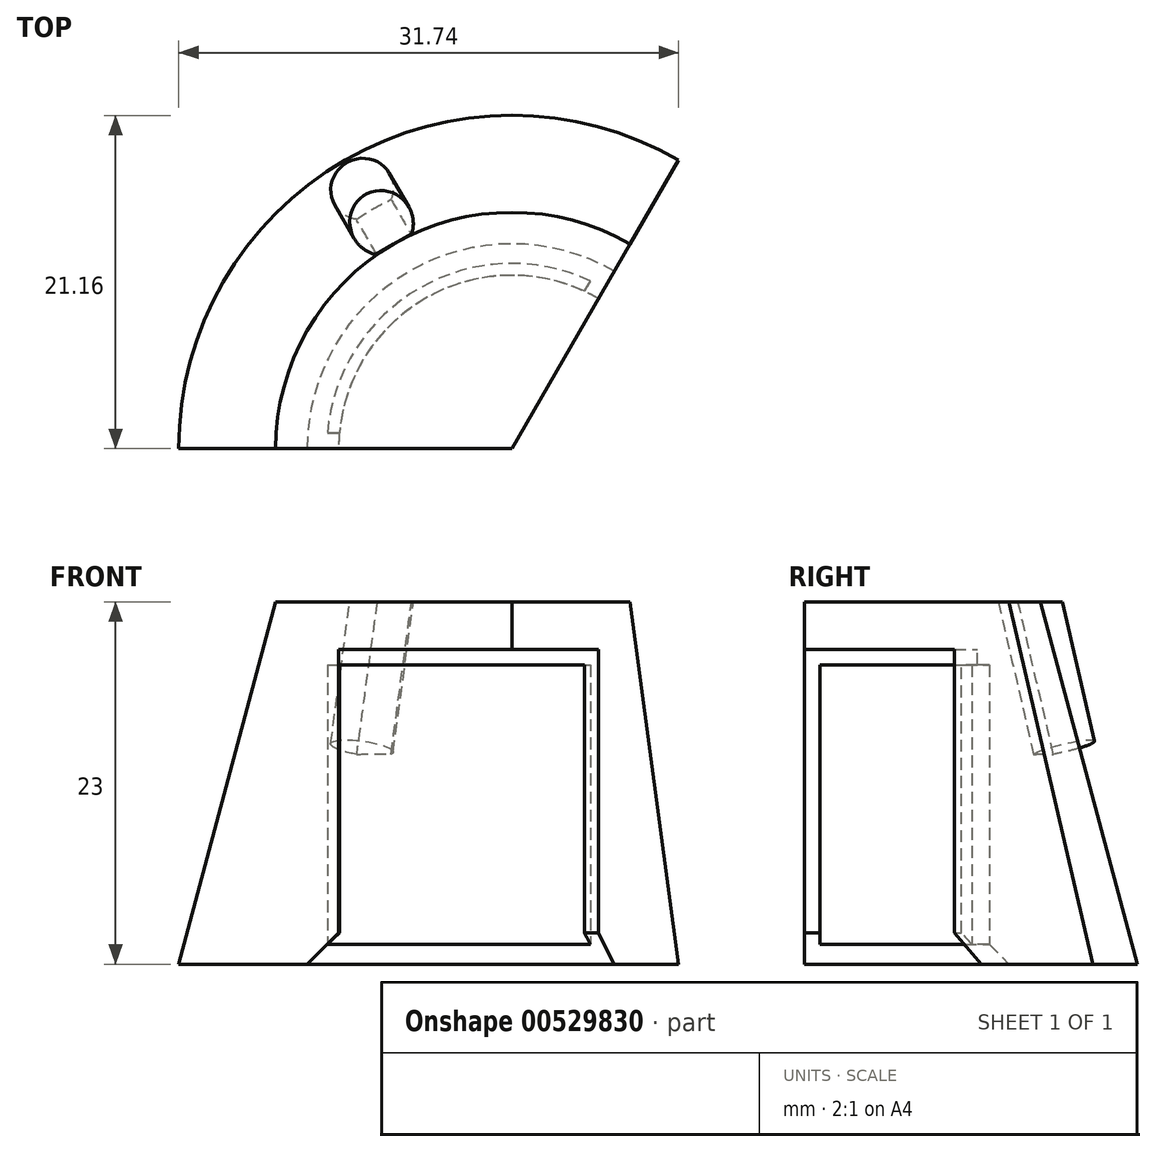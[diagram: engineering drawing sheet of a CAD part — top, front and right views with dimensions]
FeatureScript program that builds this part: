
annotation { "Feature Type Name" : "Feature", "Feature Type Description" : "" }
export const myFeature = defineFeature(function(context is Context, id is Id, definition is map)
    precondition{}
    {
        {
            var Q0;
            Q0=qCreatedBy(makeId("Front.planeOp"),FACE);
            var sketch = newSketch(context, id + "F0", { "sketchPlane" : qUnion([Q0])});
            skLineSegment(sketch, "E0", {"start": v(0, 0) * mm, "end": v(0, -3) * mm});
            skLineSegment(sketch, "E1", {"start": v(0, -3) * mm, "end": v(-11, -3) * mm});
            skLineSegment(sketch, "E2", {"start": v(-11, -3) * mm, "end": v(-11, -21) * mm});
            skLineSegment(sketch, "E3", {"start": v(0, 0) * mm, "end": v(-15, 0) * mm});
            skLineSegment(sketch, "E4", {"start": v(-13, -23) * mm, "end": v(-21.16, -23) * mm});
            skLineSegment(sketch, "E5", {"start": v(-15, 0) * mm, "end": v(-21.16, -23) * mm});
            skLineSegment(sketch, "E6", {"start": v(-11, -21) * mm, "end": v(-13, -23) * mm});
            skSolve(sketch);
        }
        {
            var Q0;
            Q0=makeQuery(id+"F0.imprint","IMPRINT",FACE,{"disambiguationData":[TD([[makeQuery(id+"F0.imprint","IMPRINT",EDGE,{"derivedFrom":sQuery(id+"F0.wireOp",EDGE,"E0")}),-1.0]])]});
            var Q1;
            Q1=sQuery(id+"F0.wireOp",EDGE,"E0");
            revolve(context, id + "F1", {"entities" : qUnion([Q0]), "axis" : qUnion([Q1]), "revolveType" : RevolveType.ONE_DIRECTION, "angle" : 120 * degree});
        }
        {
            var Q0;
            Q0=makeQuery(id+"F1.opRevolve","SWEPT_FACE",FACE,{"disambiguationData":[OSD([sQuery(id+"F0.wireOp",EDGE,"E3")])]});
            var sketch = newSketch(context, id + "F2", { "sketchPlane" : qUnion([Q0])});
            skLineSegment(sketch, "E7", {"start": v(-3.98, 15.02) * mm, "end": v(-11.37, 10.76) * mm, "construction": true});
            skLineSegment(sketch, "E8", {"start": v(-15, 0) * mm, "end": v(7.5, 13) * mm, "construction": true});
            skPoint(sketch, "E9", {"position": v(-7.5, 13) * mm});
            skSolve(sketch);
        }
        {
            var Q0;
            Q0=sQuery(id+"F2.wireOp",EDGE,"E7");
            var Q1;
            {var subQ0=sQuery(id+"F0.wireOp",EDGE,"E3");Q1=makeQuery(id+"F2.imprint","IMPRINT",FACE,{"disambiguationData":[TD([[makeQuery(id+"F2.imprint","IMPRINT",EDGE,{"derivedFrom":makeQuery(id+"F1.opRevolve","CAP_EDGE",EDGE,{"disambiguationData":[OSD([subQ0])],"isStart":true})}),-1.0]])]});}
            cPlane(context, id + "F3", {"entities" : qUnion([Q0, Q1]), "cplaneType" : CPlaneType.LINE_ANGLE, "offset" : 25 * mm, "angle" : 15 * degree, "oppositeDirection" : true, "width" : 150 * mm, "height" : 150 * mm});
        }
        {
            var Q0;
            Q0=qCreatedBy(id+"F3.planeOp",FACE);
            var sketch = newSketch(context, id + "F4", { "sketchPlane" : qUnion([Q0])});
            skPoint(sketch, "E10.0", {"position": v(-7.06, -12.65) * mm});
            skLineSegment(sketch, "E11", {"start": v(-7.06, -12.65) * mm, "end": v(-7.79, -13.96) * mm});
            skCircle(sketch, "E12", {"center": v(-7.79, -13.96) * mm, "radius": 2 * mm});
            skSolve(sketch);
        }
        {
            var Q0;
            Q0=makeQuery(id+"F4.imprint","IMPRINT",FACE,{"disambiguationData":[TD([[makeQuery(id+"F4.imprint","IMPRINT",EDGE,{"derivedFrom":sQuery(id+"F4.wireOp",EDGE,"E12")}),1.0]])]});
            extrude(context, id + "F5", {"entities" : qUnion([Q0]), "operationType" : NewBodyOperationType.ADD, "depth" : 10 * mm, "offsetDistance" : 25 * mm});
        }
        {
            var Q0;
            {var subQ0=sQuery(id+"F0.wireOp",EDGE,"E3");Q0=makeQuery(id+"F2.imprint","IMPRINT",FACE,{"disambiguationData":[TD([[makeQuery(id+"F2.imprint","IMPRINT",EDGE,{"derivedFrom":makeQuery(id+"F1.opRevolve","CAP_EDGE",EDGE,{"disambiguationData":[OSD([subQ0])],"isStart":true})}),-1.0]])]});}
            var sketch = newSketch(context, id + "F6", { "sketchPlane" : qUnion([Q0])});
            skLineSegment(sketch, "E13.bottom", {"start": v(0, 0) * mm, "end": v(-15, 0) * mm});
            skLineSegment(sketch, "E13.top", {"start": v(0, 20) * mm, "end": v(-15, 20) * mm});
            skLineSegment(sketch, "E13.left", {"start": v(0, 0) * mm, "end": v(0, 20) * mm});
            skLineSegment(sketch, "E13.right", {"start": v(-15, 0) * mm, "end": v(-15, 20) * mm});
            skSolve(sketch);
        }
        {
            var Q0;
            {var subQ0=sQuery(id+"F6.wireOp",EDGE,"E13.top");Q0=makeQuery(id+"F6.imprint","IMPRINT",FACE,{"disambiguationData":[TD([[makeQuery(id+"F6.imprint","IMPRINT",EDGE,{"derivedFrom":subQ0}),1.0]])]});}
            extrude(context, id + "F7", {"entities" : qUnion([Q0]), "operationType" : NewBodyOperationType.REMOVE, "depth" : 25 * mm, "offsetDistance" : 25 * mm});
        }
        {
            var Q0;
            Q0=makeQuery(id+"F1.opRevolve","SWEPT_FACE",FACE,{"disambiguationData":[OSD([sQuery(id+"F0.wireOp",EDGE,"E4")])]});
            var sketch = newSketch(context, id + "F8", { "sketchPlane" : qUnion([Q0])});
            skArc(sketch, "E14", {"start": v(-11.7, -1) * mm, "mid": v(-5.88, -10.18) * mm, "end": v(4.99, -10.64) * mm});
            skLineSegment(sketch, "E15", {"start": v(-11.7, -1) * mm, "end": v(-10.45, -1) * mm});
            skLineSegment(sketch, "E16", {"start": v(4.36, -9.55) * mm, "end": v(4.99, -10.64) * mm});
            skArc(sketch, "E17", {"start": v(-10.45, -1) * mm, "mid": v(-5.25, -9.1) * mm, "end": v(4.36, -9.55) * mm});
            skSolve(sketch);
        }
        {
            var Q0;
            {var subQ0=sQuery(id+"F8.wireOp",EDGE,"E14");Q0=makeQuery(id+"F8.imprint","IMPRINT",FACE,{"disambiguationData":[TD([[makeQuery(id+"F8.imprint","IMPRINT",EDGE,{"derivedFrom":subQ0}),1.0]])]});}
            extrude(context, id + "F9", {"entities" : qUnion([Q0]), "operationType" : NewBodyOperationType.REMOVE, "oppositeDirection" : true, "depth" : 19 * mm, "offsetDistance" : 25 * mm});
        }
    });
